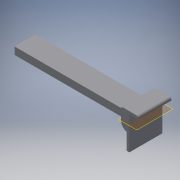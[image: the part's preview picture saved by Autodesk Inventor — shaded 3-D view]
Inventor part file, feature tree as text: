
AUTODESK INVENTOR PART (.ipt)
format: ipt  version: 2018 (Build 220112000, 112)  size: 173,568 bytes
history: native  units: in
note: dims shown in document units (in); Inventor stores cm internally (conversion verified against a paired STEP export)
features: extrude x6, sketch x6, fillet x3, plane x1
ambient origin geometry x8: Origin, YZ Plane, XZ Plane, XY Plane, X Axis, Y Axis, Z Axis, Center Point
bodies: Solid1 (feature_tree)
feature tree (16):
  extrude  "Extrusion1"  Depth=0.6in
  plane  "Work Plane1"
  extrude  "Extrusion2"  Depth=0.05in TaperAngle=0.0deg
  extrude  "Extrusion3"  Depth=0.05in TaperAngle=0.0deg
  extrude  "Extrusion4"  Depth=0.05in TaperAngle=0.0deg
  extrude  "Extrusion5"  Depth=0.3in
  extrude  "Extrusion6"  Depth=0.125in
  fillet  "Fillet1"  Radius=0.0394in
  fillet  "Fillet2"  Radius=0.0394in
  fillet  "Fillet3"  [1 undecoded]
  sketch  "Sketch1"  dims[d0=0.3in d1=0.6in]
  sketch  "Sketch3"  dims[d2=0.3in d3=0.0in d4=0.05in d5=0.0in]
  sketch  "Sketch4"  dims[d6=2.0in d7=0.05in d8=0.0in]
  sketch  "Sketch5"  dims[d9=0.15in d10=0.0in d11=0.05in d12=0.0in]
  sketch  "Sketch6"  dims[d13=0.05in d14=0.3in]
  sketch  "Sketch7"  dims[d15=0.05in d16=0.0in d17=0.125in d18=0.0394in d19=0.0394in]
note: 1 required parameter value undecoded (feature->parameter linkage not recoverable at this tier; creation-order binding heuristic only, values carry confidence <= 0.55)
